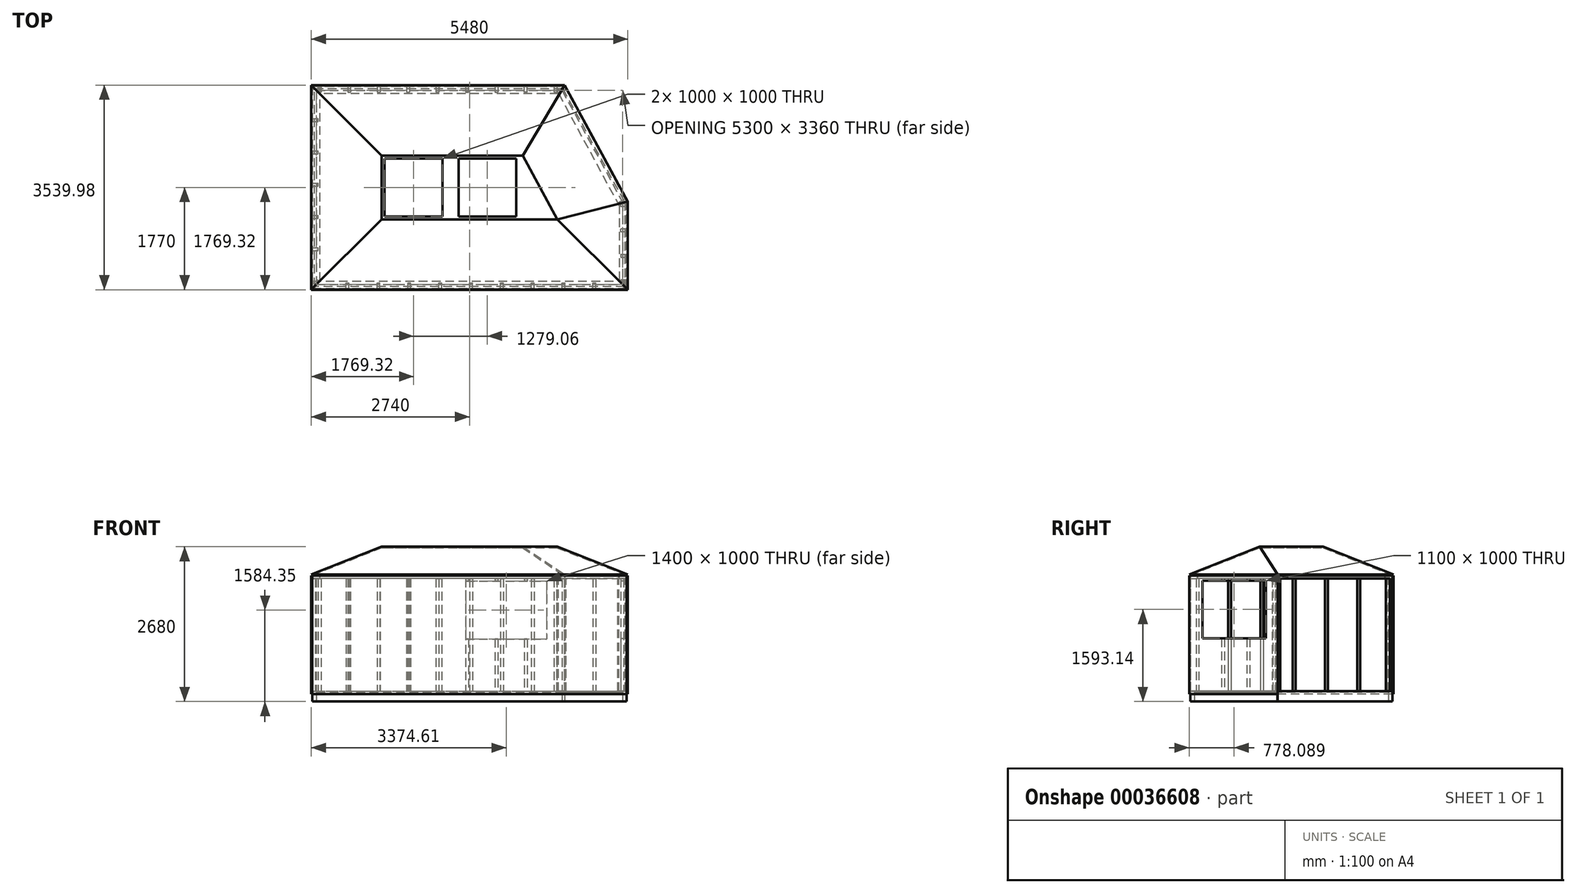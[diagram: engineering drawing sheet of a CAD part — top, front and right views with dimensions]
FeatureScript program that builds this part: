
annotation { "Feature Type Name" : "Feature", "Feature Type Description" : "" }
export const myFeature = defineFeature(function(context is Context, id is Id, definition is map)
    precondition{}
    {
        {
            var Q0;
            Q0=qCreatedBy(makeId("Top.planeOp"),FACE);
            var sketch = newSketch(context, id + "F0", { "sketchPlane" : qUnion([Q0])});
            skLineSegment(sketch, "E0.bottom", {"start": v(0, 0) * mm, "end": v(4365, 0) * mm});
            skLineSegment(sketch, "E0.top", {"start": v(0, -3500) * mm, "end": v(5440, -3500) * mm});
            skLineSegment(sketch, "E0.left", {"start": v(0, 0) * mm, "end": v(0, -3500) * mm});
            skLineSegment(sketch, "E0.right", {"start": v(5440, -1990) * mm, "end": v(5440, -3500) * mm});
            skLineSegment(sketch, "E1", {"start": v(4365, 0) * mm, "end": v(5440, -1990) * mm});
            skLineSegment(sketch, "E2.0", {"start": v(70, -70) * mm, "end": v(70, -3430) * mm});
            skLineSegment(sketch, "E2.1", {"start": v(70, -70) * mm, "end": v(4323.25, -70) * mm});
            skLineSegment(sketch, "E2.2", {"start": v(4323.25, -70) * mm, "end": v(5370, -2007.7) * mm});
            skLineSegment(sketch, "E2.3", {"start": v(5370, -2007.7) * mm, "end": v(5370, -3430) * mm});
            skLineSegment(sketch, "E2.4", {"start": v(70, -3430) * mm, "end": v(5370, -3430) * mm});
            skSolve(sketch);
        }
        {
            var Q0;
            Q0=makeQuery(id+"F0.imprint","IMPRINT",FACE,{"disambiguationData":[TD([[makeQuery(id+"F0.imprint","IMPRINT",EDGE,{"derivedFrom":sQuery(id+"F0.wireOp",EDGE,"E0.bottom")}),-1.0]])]});
            extrude(context, id + "F1", {"entities" : qUnion([Q0]), "depth" : 180 * mm});
        }
        {
            var Q0;
            Q0=makeQuery(id+"F0.imprint","IMPRINT",FACE,{"disambiguationData":[TD([[makeQuery(id+"F0.imprint","IMPRINT",EDGE,{"derivedFrom":sQuery(id+"F0.wireOp",EDGE,"E2.0")}),1.0]])]});
            extrude(context, id + "F2", {"entities" : qUnion([Q0]), "depth" : 180 * mm, "hasSecondDirection" : true, "secondDirectionOppositeDirection" : false, "secondDirectionDepth" : 160 * mm});
        }
        {
            var Q0;
            Q0=makeQuery(id+"F1.opExtrude","CAP_FACE",FACE,{"disambiguationData":[OSD([sQuery(id+"F0.wireOp",EDGE,"E0.bottom"),sQuery(id+"F0.wireOp",EDGE,"E0.top"),sQuery(id+"F0.wireOp",EDGE,"E0.left"),sQuery(id+"F0.wireOp",EDGE,"E0.right"),sQuery(id+"F0.wireOp",EDGE,"E1"),sQuery(id+"F0.wireOp",EDGE,"E2.0"),sQuery(id+"F0.wireOp",EDGE,"E2.1"),sQuery(id+"F0.wireOp",EDGE,"E2.2"),sQuery(id+"F0.wireOp",EDGE,"E2.3"),sQuery(id+"F0.wireOp",EDGE,"E2.4")])],"isStart":false});
            var sketch = newSketch(context, id + "F3", { "sketchPlane" : qUnion([Q0])});
            skLineSegment(sketch, "E3.bottom", {"start": v(0, -3500) * mm, "end": v(50, -3500) * mm});
            skLineSegment(sketch, "E3.top", {"start": v(0, -3400) * mm, "end": v(50, -3400) * mm});
            skLineSegment(sketch, "E3.left", {"start": v(0, -3500) * mm, "end": v(0, -3400) * mm});
            skLineSegment(sketch, "E3.right", {"start": v(50, -3500) * mm, "end": v(50, -3400) * mm});
            skLineSegment(sketch, "E4.bottom", {"start": v(50, -3500) * mm, "end": v(100, -3500) * mm});
            skLineSegment(sketch, "E4.top", {"start": v(50, -3400) * mm, "end": v(100, -3400) * mm});
            skLineSegment(sketch, "E4.right", {"start": v(100, -3500) * mm, "end": v(100, -3400) * mm});
            skLineSegment(sketch, "E5.1.0.0", {"start": v(584, -3400) * mm, "end": v(634, -3400) * mm});
            skLineSegment(sketch, "E5.1.0.1", {"start": v(584, -3500) * mm, "end": v(584, -3400) * mm});
            skLineSegment(sketch, "E5.1.0.2", {"start": v(584, -3500) * mm, "end": v(634, -3500) * mm});
            skLineSegment(sketch, "E5.1.0.3", {"start": v(634, -3500) * mm, "end": v(634, -3400) * mm});
            skLineSegment(sketch, "E5.2.0.0", {"start": v(1118, -3400) * mm, "end": v(1168, -3400) * mm});
            skLineSegment(sketch, "E5.2.0.1", {"start": v(1118, -3500) * mm, "end": v(1118, -3400) * mm});
            skLineSegment(sketch, "E5.2.0.2", {"start": v(1118, -3500) * mm, "end": v(1168, -3500) * mm});
            skLineSegment(sketch, "E5.2.0.3", {"start": v(1168, -3500) * mm, "end": v(1168, -3400) * mm});
            skLineSegment(sketch, "E5.3.0.0", {"start": v(1652, -3400) * mm, "end": v(1702, -3400) * mm});
            skLineSegment(sketch, "E5.3.0.1", {"start": v(1652, -3500) * mm, "end": v(1652, -3400) * mm});
            skLineSegment(sketch, "E5.3.0.2", {"start": v(1652, -3500) * mm, "end": v(1702, -3500) * mm});
            skLineSegment(sketch, "E5.3.0.3", {"start": v(1702, -3500) * mm, "end": v(1702, -3400) * mm});
            skLineSegment(sketch, "E5.4.0.0", {"start": v(2186, -3400) * mm, "end": v(2236, -3400) * mm});
            skLineSegment(sketch, "E5.4.0.1", {"start": v(2186, -3500) * mm, "end": v(2186, -3400) * mm});
            skLineSegment(sketch, "E5.4.0.2", {"start": v(2186, -3500) * mm, "end": v(2236, -3500) * mm});
            skLineSegment(sketch, "E5.4.0.3", {"start": v(2236, -3500) * mm, "end": v(2236, -3400) * mm});
            skLineSegment(sketch, "E5.5.0.0", {"start": v(2720, -3400) * mm, "end": v(2770, -3400) * mm});
            skLineSegment(sketch, "E5.5.0.1", {"start": v(2720, -3500) * mm, "end": v(2720, -3400) * mm});
            skLineSegment(sketch, "E5.5.0.2", {"start": v(2720, -3500) * mm, "end": v(2770, -3500) * mm});
            skLineSegment(sketch, "E5.5.0.3", {"start": v(2770, -3500) * mm, "end": v(2770, -3400) * mm});
            skLineSegment(sketch, "E5.6.0.0", {"start": v(3254, -3400) * mm, "end": v(3304, -3400) * mm});
            skLineSegment(sketch, "E5.6.0.1", {"start": v(3254, -3500) * mm, "end": v(3254, -3400) * mm});
            skLineSegment(sketch, "E5.6.0.2", {"start": v(3254, -3500) * mm, "end": v(3304, -3500) * mm});
            skLineSegment(sketch, "E5.6.0.3", {"start": v(3304, -3500) * mm, "end": v(3304, -3400) * mm});
            skLineSegment(sketch, "E5.7.0.0", {"start": v(3788, -3400) * mm, "end": v(3838, -3400) * mm});
            skLineSegment(sketch, "E5.7.0.1", {"start": v(3788, -3500) * mm, "end": v(3788, -3400) * mm});
            skLineSegment(sketch, "E5.7.0.2", {"start": v(3788, -3500) * mm, "end": v(3838, -3500) * mm});
            skLineSegment(sketch, "E5.7.0.3", {"start": v(3838, -3500) * mm, "end": v(3838, -3400) * mm});
            skLineSegment(sketch, "E5.8.0.0", {"start": v(4322, -3400) * mm, "end": v(4372, -3400) * mm});
            skLineSegment(sketch, "E5.8.0.1", {"start": v(4322, -3500) * mm, "end": v(4322, -3400) * mm});
            skLineSegment(sketch, "E5.8.0.2", {"start": v(4322, -3500) * mm, "end": v(4372, -3500) * mm});
            skLineSegment(sketch, "E5.8.0.3", {"start": v(4372, -3500) * mm, "end": v(4372, -3400) * mm});
            skLineSegment(sketch, "E5.9.0.0", {"start": v(4856, -3400) * mm, "end": v(4906, -3400) * mm});
            skLineSegment(sketch, "E5.9.0.1", {"start": v(4856, -3500) * mm, "end": v(4856, -3400) * mm});
            skLineSegment(sketch, "E5.9.0.2", {"start": v(4856, -3500) * mm, "end": v(4906, -3500) * mm});
            skLineSegment(sketch, "E5.9.0.3", {"start": v(4906, -3500) * mm, "end": v(4906, -3400) * mm});
            skLineSegment(sketch, "E5.10.0.0", {"start": v(5390, -3400) * mm, "end": v(5440, -3400) * mm});
            skLineSegment(sketch, "E5.10.0.1", {"start": v(5390, -3500) * mm, "end": v(5390, -3400) * mm});
            skLineSegment(sketch, "E5.10.0.2", {"start": v(5390, -3500) * mm, "end": v(5440, -3500) * mm});
            skLineSegment(sketch, "E5.10.0.3", {"start": v(5440, -3500) * mm, "end": v(5440, -3400) * mm});
            skLineSegment(sketch, "E5.direction1", {"start": v(50, -3500) * mm, "end": v(584, -3500) * mm, "construction": true});
            skLineSegment(sketch, "E6.bottom", {"start": v(5440, -3500) * mm, "end": v(0, -3500) * mm});
            skLineSegment(sketch, "E6.top", {"start": v(5440, -3520) * mm, "end": v(0, -3520) * mm});
            skLineSegment(sketch, "E6.left", {"start": v(5440, -3500) * mm, "end": v(5440, -3520) * mm});
            skLineSegment(sketch, "E6.right", {"start": v(0, -3500) * mm, "end": v(0, -3520) * mm});
            skLineSegment(sketch, "E7.bottom", {"start": v(0, -3400) * mm, "end": v(100, -3400) * mm});
            skLineSegment(sketch, "E7.top", {"start": v(0, -3350) * mm, "end": v(100, -3350) * mm});
            skLineSegment(sketch, "E7.left", {"start": v(0, -3400) * mm, "end": v(0, -3350) * mm});
            skLineSegment(sketch, "E7.right", {"start": v(100, -3400) * mm, "end": v(100, -3350) * mm});
            skLineSegment(sketch, "E8.0.1.0", {"start": v(0, -2841.67) * mm, "end": v(0, -2791.67) * mm});
            skLineSegment(sketch, "E8.0.1.1", {"start": v(100, -2841.67) * mm, "end": v(100, -2791.67) * mm});
            skLineSegment(sketch, "E8.0.1.2", {"start": v(0, -2841.67) * mm, "end": v(100, -2841.67) * mm});
            skLineSegment(sketch, "E8.0.1.3", {"start": v(0, -2791.67) * mm, "end": v(100, -2791.67) * mm});
            skLineSegment(sketch, "E8.0.2.0", {"start": v(0, -2283.34) * mm, "end": v(0, -2233.34) * mm});
            skLineSegment(sketch, "E8.0.2.1", {"start": v(100, -2283.34) * mm, "end": v(100, -2233.34) * mm});
            skLineSegment(sketch, "E8.0.2.2", {"start": v(0, -2283.34) * mm, "end": v(100, -2283.34) * mm});
            skLineSegment(sketch, "E8.0.2.3", {"start": v(0, -2233.34) * mm, "end": v(100, -2233.34) * mm});
            skLineSegment(sketch, "E8.0.3.0", {"start": v(0, -1725) * mm, "end": v(0, -1675) * mm});
            skLineSegment(sketch, "E8.0.3.1", {"start": v(100, -1725) * mm, "end": v(100, -1675) * mm});
            skLineSegment(sketch, "E8.0.3.2", {"start": v(0, -1725) * mm, "end": v(100, -1725) * mm});
            skLineSegment(sketch, "E8.0.3.3", {"start": v(0, -1675) * mm, "end": v(100, -1675) * mm});
            skLineSegment(sketch, "E8.0.4.0", {"start": v(0, -1166.68) * mm, "end": v(0, -1116.68) * mm});
            skLineSegment(sketch, "E8.0.4.1", {"start": v(100, -1166.68) * mm, "end": v(100, -1116.68) * mm});
            skLineSegment(sketch, "E8.0.4.2", {"start": v(0, -1166.68) * mm, "end": v(100, -1166.68) * mm});
            skLineSegment(sketch, "E8.0.4.3", {"start": v(0, -1116.68) * mm, "end": v(100, -1116.68) * mm});
            skLineSegment(sketch, "E8.0.5.0", {"start": v(0, -608.35) * mm, "end": v(0, -558.35) * mm});
            skLineSegment(sketch, "E8.0.5.1", {"start": v(100, -608.35) * mm, "end": v(100, -558.35) * mm});
            skLineSegment(sketch, "E8.0.5.2", {"start": v(0, -608.35) * mm, "end": v(100, -608.35) * mm});
            skLineSegment(sketch, "E8.0.5.3", {"start": v(0, -558.35) * mm, "end": v(100, -558.35) * mm});
            skLineSegment(sketch, "E8.0.6.0", {"start": v(0, -50.02) * mm, "end": v(0, -0.02) * mm});
            skLineSegment(sketch, "E8.0.6.1", {"start": v(100, -50.02) * mm, "end": v(100, -0.02) * mm});
            skLineSegment(sketch, "E8.0.6.2", {"start": v(0, -50.02) * mm, "end": v(100, -50.02) * mm});
            skLineSegment(sketch, "E8.0.6.3", {"start": v(0, -0.02) * mm, "end": v(100, -0.02) * mm});
            skLineSegment(sketch, "E8.direction1", {"start": v(0, -3400) * mm, "end": v(133.01, -3400) * mm, "construction": true});
            skLineSegment(sketch, "E8.direction2", {"start": v(0, -3400) * mm, "end": v(0, -2841.67) * mm, "construction": true});
            skLineSegment(sketch, "E9.bottom", {"start": v(-20, -0.02) * mm, "end": v(0, -0.02) * mm});
            skLineSegment(sketch, "E9.top", {"start": v(-20, -3520) * mm, "end": v(0, -3520) * mm});
            skLineSegment(sketch, "E9.left", {"start": v(-20, -0.02) * mm, "end": v(-20, -3520) * mm});
            skLineSegment(sketch, "E9.right", {"start": v(0, -0.02) * mm, "end": v(0, -3520) * mm});
            skSolve(sketch);
        }
        {
            var Q0;
            Q0=makeQuery(id+"F3.imprint","IMPRINT",FACE,{"disambiguationData":[TD([[makeQuery(id+"F3.imprint","IMPRINT",EDGE,{"derivedFrom":sQuery(id+"F3.wireOp",EDGE,"E5.10.0.0")}),-1.0]])]});
            var Q1;
            {var subQ3=sQuery(id+"F3.wireOp",EDGE,"E5.9.0.1");var subQ5=sQuery(id+"F3.wireOp",EDGE,"E6.bottom");var subQ7=makeQuery(id+"F3.imprint","INTERSECT",VERTEX,{"derivedFrom":[subQ3,subQ5]});Q1=makeQuery(id+"F3.imprint","IMPRINT",FACE,{"disambiguationData":[TD([[makeQuery(id+"F3.imprint","IMPRINT",EDGE,{"disambiguationData":[TD([[subQ7,-1.0]])],"derivedFrom":subQ3}),-1.0]])]});}
            var Q2;
            {var subQ3=sQuery(id+"F3.wireOp",EDGE,"E5.9.0.0");Q2=makeQuery(id+"F3.imprint","IMPRINT",FACE,{"disambiguationData":[TD([[makeQuery(id+"F3.imprint","IMPRINT",EDGE,{"derivedFrom":subQ3}),-1.0]])]});}
            var Q3;
            {var subQ3=sQuery(id+"F3.wireOp",EDGE,"E5.8.0.1");var subQ5=sQuery(id+"F3.wireOp",EDGE,"E6.bottom");var subQ7=makeQuery(id+"F3.imprint","INTERSECT",VERTEX,{"derivedFrom":[subQ3,subQ5]});Q3=makeQuery(id+"F3.imprint","IMPRINT",FACE,{"disambiguationData":[TD([[makeQuery(id+"F3.imprint","IMPRINT",EDGE,{"disambiguationData":[TD([[subQ7,-1.0]])],"derivedFrom":subQ3}),-1.0]])]});}
            var Q4;
            {var subQ5=sQuery(id+"F3.wireOp",EDGE,"E5.8.0.0");Q4=makeQuery(id+"F3.imprint","IMPRINT",FACE,{"disambiguationData":[TD([[makeQuery(id+"F3.imprint","IMPRINT",EDGE,{"derivedFrom":subQ5}),-1.0]])]});}
            var Q5;
            {var subQ0=sQuery(id+"F3.wireOp",EDGE,"E6.bottom");var subQ3=sQuery(id+"F3.wireOp",EDGE,"E5.7.0.1");var subQ4=makeQuery(id+"F3.imprint","INTERSECT",VERTEX,{"derivedFrom":[subQ3,subQ0]});Q5=makeQuery(id+"F3.imprint","IMPRINT",FACE,{"disambiguationData":[TD([[makeQuery(id+"F3.imprint","IMPRINT",EDGE,{"disambiguationData":[TD([[subQ4,-1.0]])],"derivedFrom":subQ3}),-1.0]])]});}
            var Q6;
            {var subQ3=sQuery(id+"F3.wireOp",EDGE,"E5.7.0.0");Q6=makeQuery(id+"F3.imprint","IMPRINT",FACE,{"disambiguationData":[TD([[makeQuery(id+"F3.imprint","IMPRINT",EDGE,{"derivedFrom":subQ3}),-1.0]])]});}
            var Q7;
            {var subQ3=sQuery(id+"F3.wireOp",EDGE,"E5.6.0.1");var subQ5=sQuery(id+"F3.wireOp",EDGE,"E6.bottom");var subQ7=makeQuery(id+"F3.imprint","INTERSECT",VERTEX,{"derivedFrom":[subQ3,subQ5]});Q7=makeQuery(id+"F3.imprint","IMPRINT",FACE,{"disambiguationData":[TD([[makeQuery(id+"F3.imprint","IMPRINT",EDGE,{"disambiguationData":[TD([[subQ7,-1.0]])],"derivedFrom":subQ3}),-1.0]])]});}
            var Q8;
            {var subQ5=sQuery(id+"F3.wireOp",EDGE,"E5.6.0.0");Q8=makeQuery(id+"F3.imprint","IMPRINT",FACE,{"disambiguationData":[TD([[makeQuery(id+"F3.imprint","IMPRINT",EDGE,{"derivedFrom":subQ5}),-1.0]])]});}
            var Q9;
            {var subQ3=sQuery(id+"F3.wireOp",EDGE,"E5.5.0.1");var subQ5=sQuery(id+"F3.wireOp",EDGE,"E6.bottom");var subQ7=makeQuery(id+"F3.imprint","INTERSECT",VERTEX,{"derivedFrom":[subQ3,subQ5]});Q9=makeQuery(id+"F3.imprint","IMPRINT",FACE,{"disambiguationData":[TD([[makeQuery(id+"F3.imprint","IMPRINT",EDGE,{"disambiguationData":[TD([[subQ7,-1.0]])],"derivedFrom":subQ3}),-1.0]])]});}
            var Q10;
            {var subQ5=sQuery(id+"F3.wireOp",EDGE,"E5.5.0.0");Q10=makeQuery(id+"F3.imprint","IMPRINT",FACE,{"disambiguationData":[TD([[makeQuery(id+"F3.imprint","IMPRINT",EDGE,{"derivedFrom":subQ5}),-1.0]])]});}
            var Q11;
            {var subQ3=sQuery(id+"F3.wireOp",EDGE,"E5.4.0.1");var subQ5=sQuery(id+"F3.wireOp",EDGE,"E6.bottom");var subQ7=makeQuery(id+"F3.imprint","INTERSECT",VERTEX,{"derivedFrom":[subQ3,subQ5]});Q11=makeQuery(id+"F3.imprint","IMPRINT",FACE,{"disambiguationData":[TD([[makeQuery(id+"F3.imprint","IMPRINT",EDGE,{"disambiguationData":[TD([[subQ7,-1.0]])],"derivedFrom":subQ3}),-1.0]])]});}
            var Q12;
            {var subQ5=sQuery(id+"F3.wireOp",EDGE,"E5.4.0.0");Q12=makeQuery(id+"F3.imprint","IMPRINT",FACE,{"disambiguationData":[TD([[makeQuery(id+"F3.imprint","IMPRINT",EDGE,{"derivedFrom":subQ5}),-1.0]])]});}
            var Q13;
            {var subQ3=sQuery(id+"F3.wireOp",EDGE,"E5.3.0.1");var subQ5=sQuery(id+"F3.wireOp",EDGE,"E6.bottom");var subQ7=makeQuery(id+"F3.imprint","INTERSECT",VERTEX,{"derivedFrom":[subQ3,subQ5]});Q13=makeQuery(id+"F3.imprint","IMPRINT",FACE,{"disambiguationData":[TD([[makeQuery(id+"F3.imprint","IMPRINT",EDGE,{"disambiguationData":[TD([[subQ7,-1.0]])],"derivedFrom":subQ3}),-1.0]])]});}
            var Q14;
            {var subQ5=sQuery(id+"F3.wireOp",EDGE,"E5.3.0.0");Q14=makeQuery(id+"F3.imprint","IMPRINT",FACE,{"disambiguationData":[TD([[makeQuery(id+"F3.imprint","IMPRINT",EDGE,{"derivedFrom":subQ5}),-1.0]])]});}
            var Q15;
            {var subQ3=sQuery(id+"F3.wireOp",EDGE,"E5.2.0.1");var subQ5=sQuery(id+"F3.wireOp",EDGE,"E6.bottom");var subQ7=makeQuery(id+"F3.imprint","INTERSECT",VERTEX,{"derivedFrom":[subQ3,subQ5]});Q15=makeQuery(id+"F3.imprint","IMPRINT",FACE,{"disambiguationData":[TD([[makeQuery(id+"F3.imprint","IMPRINT",EDGE,{"disambiguationData":[TD([[subQ7,-1.0]])],"derivedFrom":subQ3}),-1.0]])]});}
            var Q16;
            {var subQ5=sQuery(id+"F3.wireOp",EDGE,"E5.2.0.0");Q16=makeQuery(id+"F3.imprint","IMPRINT",FACE,{"disambiguationData":[TD([[makeQuery(id+"F3.imprint","IMPRINT",EDGE,{"derivedFrom":subQ5}),-1.0]])]});}
            var Q17;
            {var subQ0=sQuery(id+"F3.wireOp",EDGE,"E6.bottom");var subQ3=sQuery(id+"F3.wireOp",EDGE,"E5.1.0.1");var subQ4=makeQuery(id+"F3.imprint","INTERSECT",VERTEX,{"derivedFrom":[subQ3,subQ0]});Q17=makeQuery(id+"F3.imprint","IMPRINT",FACE,{"disambiguationData":[TD([[makeQuery(id+"F3.imprint","IMPRINT",EDGE,{"disambiguationData":[TD([[subQ4,-1.0]])],"derivedFrom":subQ3}),-1.0]])]});}
            var Q18;
            {var subQ5=sQuery(id+"F3.wireOp",EDGE,"E5.1.0.0");Q18=makeQuery(id+"F3.imprint","IMPRINT",FACE,{"disambiguationData":[TD([[makeQuery(id+"F3.imprint","IMPRINT",EDGE,{"derivedFrom":subQ5}),-1.0]])]});}
            extrude(context, id + "F4", {"entities" : qUnion([Q0, Q1, Q2, Q3, Q4, Q5, Q6, Q7, Q8, Q9, Q10, Q11, Q12, Q13, Q14, Q15, Q16, Q17, Q18]), "depth" : 1950 * mm});
        }
        {
            var Q0;
            {var subQ5=sQuery(id+"F3.wireOp",EDGE,"E3.right");Q0=makeQuery(id+"F3.imprint","IMPRINT",FACE,{"disambiguationData":[TD([[makeQuery(id+"F3.imprint","IMPRINT",EDGE,{"derivedFrom":subQ5}),1.0]])]});}
            extrude(context, id + "F5", {"entities" : qUnion([Q0]), "depth" : 1950 * mm});
        }
        {
            var Q0;
            {var subQ0=sQuery(id+"F3.wireOp",EDGE,"E7.right");Q0=makeQuery(id+"F3.imprint","IMPRINT",FACE,{"disambiguationData":[TD([[makeQuery(id+"F3.imprint","IMPRINT",EDGE,{"derivedFrom":subQ0}),1.0]])]});}
            var Q1;
            {var subQ3=sQuery(id+"F3.wireOp",EDGE,"E7.bottom");var subQ5=makeQuery(id+"F3.imprint","INTERSECT",VERTEX,{"derivedFrom":[sQuery(id+"F3.wireOp",EDGE,"E3.right"),subQ3]});Q1=makeQuery(id+"F3.imprint","IMPRINT",FACE,{"disambiguationData":[TD([[makeQuery(id+"F3.imprint","IMPRINT",EDGE,{"disambiguationData":[TD([[subQ5,1.0]])],"derivedFrom":subQ3}),1.0]])]});}
            var Q2;
            {var subQ3=sQuery(id+"F3.wireOp",EDGE,"E8.0.1.2");var subQ5=sQuery(id+"F3.wireOp",EDGE,"E9.right");var subQ7=makeQuery(id+"F3.imprint","INTERSECT",VERTEX,{"derivedFrom":[subQ3,subQ5]});Q2=makeQuery(id+"F3.imprint","IMPRINT",FACE,{"disambiguationData":[TD([[makeQuery(id+"F3.imprint","IMPRINT",EDGE,{"disambiguationData":[TD([[subQ7,-1.0]])],"derivedFrom":subQ3}),1.0]])]});}
            var Q3;
            {var subQ5=sQuery(id+"F3.wireOp",EDGE,"E8.0.1.1");Q3=makeQuery(id+"F3.imprint","IMPRINT",FACE,{"disambiguationData":[TD([[makeQuery(id+"F3.imprint","IMPRINT",EDGE,{"derivedFrom":subQ5}),1.0]])]});}
            var Q4;
            {var subQ3=sQuery(id+"F3.wireOp",EDGE,"E8.0.2.2");var subQ5=sQuery(id+"F3.wireOp",EDGE,"E9.right");var subQ7=makeQuery(id+"F3.imprint","INTERSECT",VERTEX,{"derivedFrom":[subQ3,subQ5]});Q4=makeQuery(id+"F3.imprint","IMPRINT",FACE,{"disambiguationData":[TD([[makeQuery(id+"F3.imprint","IMPRINT",EDGE,{"disambiguationData":[TD([[subQ7,-1.0]])],"derivedFrom":subQ3}),1.0]])]});}
            var Q5;
            {var subQ3=sQuery(id+"F3.wireOp",EDGE,"E8.0.2.1");Q5=makeQuery(id+"F3.imprint","IMPRINT",FACE,{"disambiguationData":[TD([[makeQuery(id+"F3.imprint","IMPRINT",EDGE,{"derivedFrom":subQ3}),1.0]])]});}
            var Q6;
            {var subQ3=sQuery(id+"F3.wireOp",EDGE,"E8.0.3.2");var subQ5=sQuery(id+"F3.wireOp",EDGE,"E9.right");var subQ7=makeQuery(id+"F3.imprint","INTERSECT",VERTEX,{"derivedFrom":[subQ3,subQ5]});Q6=makeQuery(id+"F3.imprint","IMPRINT",FACE,{"disambiguationData":[TD([[makeQuery(id+"F3.imprint","IMPRINT",EDGE,{"disambiguationData":[TD([[subQ7,-1.0]])],"derivedFrom":subQ3}),1.0]])]});}
            var Q7;
            {var subQ3=sQuery(id+"F3.wireOp",EDGE,"E8.0.3.1");Q7=makeQuery(id+"F3.imprint","IMPRINT",FACE,{"disambiguationData":[TD([[makeQuery(id+"F3.imprint","IMPRINT",EDGE,{"derivedFrom":subQ3}),1.0]])]});}
            var Q8;
            {var subQ3=sQuery(id+"F3.wireOp",EDGE,"E8.0.4.2");var subQ5=sQuery(id+"F3.wireOp",EDGE,"E9.right");var subQ7=makeQuery(id+"F3.imprint","INTERSECT",VERTEX,{"derivedFrom":[subQ3,subQ5]});Q8=makeQuery(id+"F3.imprint","IMPRINT",FACE,{"disambiguationData":[TD([[makeQuery(id+"F3.imprint","IMPRINT",EDGE,{"disambiguationData":[TD([[subQ7,-1.0]])],"derivedFrom":subQ3}),1.0]])]});}
            var Q9;
            {var subQ5=sQuery(id+"F3.wireOp",EDGE,"E8.0.4.1");Q9=makeQuery(id+"F3.imprint","IMPRINT",FACE,{"disambiguationData":[TD([[makeQuery(id+"F3.imprint","IMPRINT",EDGE,{"derivedFrom":subQ5}),1.0]])]});}
            var Q10;
            {var subQ0=sQuery(id+"F3.wireOp",EDGE,"E9.right");var subQ3=sQuery(id+"F3.wireOp",EDGE,"E8.0.5.2");var subQ4=makeQuery(id+"F3.imprint","INTERSECT",VERTEX,{"derivedFrom":[subQ3,subQ0]});Q10=makeQuery(id+"F3.imprint","IMPRINT",FACE,{"disambiguationData":[TD([[makeQuery(id+"F3.imprint","IMPRINT",EDGE,{"disambiguationData":[TD([[subQ4,-1.0]])],"derivedFrom":subQ3}),1.0]])]});}
            var Q11;
            {var subQ5=sQuery(id+"F3.wireOp",EDGE,"E8.0.5.1");Q11=makeQuery(id+"F3.imprint","IMPRINT",FACE,{"disambiguationData":[TD([[makeQuery(id+"F3.imprint","IMPRINT",EDGE,{"derivedFrom":subQ5}),1.0]])]});}
            var Q12;
            Q12=makeQuery(id+"F3.imprint","IMPRINT",FACE,{"disambiguationData":[TD([[makeQuery(id+"F3.imprint","IMPRINT",EDGE,{"derivedFrom":sQuery(id+"F3.wireOp",EDGE,"E8.0.6.1")}),1.0]])]});
            extrude(context, id + "F6", {"entities" : qUnion([Q0, Q1, Q2, Q3, Q4, Q5, Q6, Q7, Q8, Q9, Q10, Q11, Q12]), "depth" : 1950 * mm});
        }
        {
            var Q0;
            {var subQ2=sQuery(id+"F3.wireOp",EDGE,"E6.top");Q0=makeQuery(id+"F3.imprint","IMPRINT",FACE,{"disambiguationData":[TD([[makeQuery(id+"F3.imprint","IMPRINT",EDGE,{"derivedFrom":subQ2}),-1.0]])]});}
            extrude(context, id + "F7", {"entities" : qUnion([Q0]), "depth" : 2000 * mm, "hasSecondDirection" : true, "secondDirectionOppositeDirection" : true, "secondDirectionDepth" : 50 * mm});
        }
        {
            var Q0;
            {var subQ9=sQuery(id+"F3.wireOp",EDGE,"E9.bottom");Q0=makeQuery(id+"F3.imprint","IMPRINT",FACE,{"disambiguationData":[TD([[makeQuery(id+"F3.imprint","IMPRINT",EDGE,{"derivedFrom":subQ9}),-1.0]])]});}
            extrude(context, id + "F8", {"entities" : qUnion([Q0]), "depth" : 2000 * mm, "hasSecondDirection" : true, "secondDirectionOppositeDirection" : true, "secondDirectionDepth" : 50 * mm});
        }
        {
            var Q0;
            Q0=makeQuery(id+"F8.opExtrude","SWEPT_FACE",FACE,{"disambiguationData":[OSD([sQuery(id+"F3.wireOp",EDGE,"E9.right")])]});
            var sketch = newSketch(context, id + "F9", { "sketchPlane" : qUnion([Q0])});
            skLineSegment(sketch, "E10.bottom", {"start": v(-3500, 2180) * mm, "end": v(-3375, 2180) * mm});
            skLineSegment(sketch, "E10.top", {"start": v(-3500, 2130) * mm, "end": v(-3375, 2130) * mm});
            skLineSegment(sketch, "E10.left", {"start": v(-3500, 2180) * mm, "end": v(-3500, 2130) * mm});
            skLineSegment(sketch, "E10.right", {"start": v(-3375, 2180) * mm, "end": v(-3375, 2130) * mm});
            skSolve(sketch);
        }
        {
            var Q0;
            Q0=makeQuery(id+"F9.imprint","IMPRINT",FACE,{"disambiguationData":[TD([[makeQuery(id+"F9.imprint","IMPRINT",EDGE,{"derivedFrom":sQuery(id+"F9.wireOp",EDGE,"E10.bottom")}),1.0]])]});
            extrude(context, id + "F10", {"entities" : qUnion([Q0]), "depth" : 5440 * mm});
        }
        {
            var Q0;
            Q0=makeQuery(id+"F10.opExtrude","SWEPT_FACE",FACE,{"disambiguationData":[OSD([sQuery(id+"F9.wireOp",EDGE,"E10.right")])]});
            var sketch = newSketch(context, id + "F11", { "sketchPlane" : qUnion([Q0])});
            skLineSegment(sketch, "E11.bottom", {"start": v(0, 2180) * mm, "end": v(-125, 2180) * mm});
            skLineSegment(sketch, "E11.top", {"start": v(0, 2130) * mm, "end": v(-125, 2130) * mm});
            skLineSegment(sketch, "E11.left", {"start": v(0, 2180) * mm, "end": v(0, 2130) * mm});
            skLineSegment(sketch, "E11.right", {"start": v(-125, 2180) * mm, "end": v(-125, 2130) * mm});
            skSolve(sketch);
        }
        {
            var Q0;
            Q0=makeQuery(id+"F11.imprint","IMPRINT",FACE,{"disambiguationData":[TD([[makeQuery(id+"F11.imprint","IMPRINT",EDGE,{"derivedFrom":sQuery(id+"F11.wireOp",EDGE,"E11.bottom")}),-1.0]])]});
            extrude(context, id + "F12", {"entities" : qUnion([Q0]), "depth" : 3375 * mm});
        }
        {
            var Q0;
            Q0=makeQuery(id+"F1.opExtrude","CAP_FACE",FACE,{"disambiguationData":[OSD([sQuery(id+"F0.wireOp",EDGE,"E0.bottom"),sQuery(id+"F0.wireOp",EDGE,"E0.top"),sQuery(id+"F0.wireOp",EDGE,"E0.left"),sQuery(id+"F0.wireOp",EDGE,"E0.right"),sQuery(id+"F0.wireOp",EDGE,"E1"),sQuery(id+"F0.wireOp",EDGE,"E2.0"),sQuery(id+"F0.wireOp",EDGE,"E2.1"),sQuery(id+"F0.wireOp",EDGE,"E2.2"),sQuery(id+"F0.wireOp",EDGE,"E2.3"),sQuery(id+"F0.wireOp",EDGE,"E2.4")])],"isStart":false});
            var sketch = newSketch(context, id + "F13", { "sketchPlane" : qUnion([Q0])});
            skLineSegment(sketch, "E12.bottom", {"start": v(100, -0.02) * mm, "end": v(150, -0.02) * mm});
            skLineSegment(sketch, "E12.top", {"start": v(100, -100.02) * mm, "end": v(150, -100.02) * mm});
            skLineSegment(sketch, "E12.left", {"start": v(100, -0.02) * mm, "end": v(100, -100.02) * mm});
            skLineSegment(sketch, "E12.right", {"start": v(150, -0.02) * mm, "end": v(150, -100.02) * mm});
            skLineSegment(sketch, "E13.1.0.0", {"start": v(610, -0.02) * mm, "end": v(660, -0.02) * mm});
            skLineSegment(sketch, "E13.1.0.1", {"start": v(610, -100.02) * mm, "end": v(660, -100.02) * mm});
            skLineSegment(sketch, "E13.1.0.2", {"start": v(610, -0.02) * mm, "end": v(610, -100.02) * mm});
            skLineSegment(sketch, "E13.1.0.3", {"start": v(660, -0.02) * mm, "end": v(660, -100.02) * mm});
            skLineSegment(sketch, "E13.2.0.0", {"start": v(1120, -0.01) * mm, "end": v(1170, -0.01) * mm});
            skLineSegment(sketch, "E13.2.0.1", {"start": v(1120, -100.01) * mm, "end": v(1170, -100.01) * mm});
            skLineSegment(sketch, "E13.2.0.2", {"start": v(1120, -0.01) * mm, "end": v(1120, -100.01) * mm});
            skLineSegment(sketch, "E13.2.0.3", {"start": v(1170, -0.01) * mm, "end": v(1170, -100.01) * mm});
            skLineSegment(sketch, "E13.3.0.0", {"start": v(1630, -0.01) * mm, "end": v(1680, -0.01) * mm});
            skLineSegment(sketch, "E13.3.0.1", {"start": v(1630, -100.01) * mm, "end": v(1680, -100.01) * mm});
            skLineSegment(sketch, "E13.3.0.2", {"start": v(1630, -0.01) * mm, "end": v(1630, -100.01) * mm});
            skLineSegment(sketch, "E13.3.0.3", {"start": v(1680, -0.01) * mm, "end": v(1680, -100.01) * mm});
            skLineSegment(sketch, "E13.4.0.0", {"start": v(2140, 0) * mm, "end": v(2190, 0) * mm});
            skLineSegment(sketch, "E13.4.0.1", {"start": v(2140, -100) * mm, "end": v(2190, -100) * mm});
            skLineSegment(sketch, "E13.4.0.2", {"start": v(2140, 0) * mm, "end": v(2140, -100) * mm});
            skLineSegment(sketch, "E13.4.0.3", {"start": v(2190, 0) * mm, "end": v(2190, -100) * mm});
            skLineSegment(sketch, "E13.5.0.0", {"start": v(2650, 0) * mm, "end": v(2700, 0) * mm});
            skLineSegment(sketch, "E13.5.0.1", {"start": v(2650, -100) * mm, "end": v(2700, -100) * mm});
            skLineSegment(sketch, "E13.5.0.2", {"start": v(2650, 0) * mm, "end": v(2650, -100) * mm});
            skLineSegment(sketch, "E13.5.0.3", {"start": v(2700, 0) * mm, "end": v(2700, -100) * mm});
            skLineSegment(sketch, "E13.6.0.0", {"start": v(3160, 0) * mm, "end": v(3210, 0) * mm});
            skLineSegment(sketch, "E13.6.0.1", {"start": v(3160, -100) * mm, "end": v(3210, -100) * mm});
            skLineSegment(sketch, "E13.6.0.2", {"start": v(3160, 0) * mm, "end": v(3160, -100) * mm});
            skLineSegment(sketch, "E13.6.0.3", {"start": v(3210, 0) * mm, "end": v(3210, -100) * mm});
            skLineSegment(sketch, "E13.7.0.0", {"start": v(3670, 0) * mm, "end": v(3720, 0) * mm});
            skLineSegment(sketch, "E13.7.0.1", {"start": v(3670, -100) * mm, "end": v(3720, -100) * mm});
            skLineSegment(sketch, "E13.7.0.2", {"start": v(3670, 0) * mm, "end": v(3670, -100) * mm});
            skLineSegment(sketch, "E13.7.0.3", {"start": v(3720, 0) * mm, "end": v(3720, -100) * mm});
            skLineSegment(sketch, "E13.8.0.0", {"start": v(4180, 0) * mm, "end": v(4230, 0) * mm});
            skLineSegment(sketch, "E13.8.0.1", {"start": v(4180, -100) * mm, "end": v(4230, -100) * mm});
            skLineSegment(sketch, "E13.8.0.2", {"start": v(4180, 0) * mm, "end": v(4180, -100) * mm});
            skLineSegment(sketch, "E13.8.0.3", {"start": v(4230, 0) * mm, "end": v(4230, -100) * mm});
            skLineSegment(sketch, "E13.direction1", {"start": v(100, -100.02) * mm, "end": v(610, -100.02) * mm, "construction": true});
            skSolve(sketch);
        }
        {
            var Q0;
            {var subQ5=sQuery(id+"F13.wireOp",EDGE,"E12.bottom");Q0=makeQuery(id+"F13.imprint","IMPRINT",FACE,{"disambiguationData":[TD([[makeQuery(id+"F13.imprint","IMPRINT",EDGE,{"derivedFrom":subQ5}),-1.0]])]});}
            var Q1;
            {var subQ5=sQuery(id+"F13.wireOp",EDGE,"E12.top");Q1=makeQuery(id+"F13.imprint","IMPRINT",FACE,{"disambiguationData":[TD([[makeQuery(id+"F13.imprint","IMPRINT",EDGE,{"derivedFrom":subQ5}),1.0]])]});}
            var Q2;
            {var subQ5=sQuery(id+"F13.wireOp",EDGE,"E13.1.0.0");Q2=makeQuery(id+"F13.imprint","IMPRINT",FACE,{"disambiguationData":[TD([[makeQuery(id+"F13.imprint","IMPRINT",EDGE,{"derivedFrom":subQ5}),-1.0]])]});}
            var Q3;
            {var subQ5=sQuery(id+"F13.wireOp",EDGE,"E13.1.0.1");Q3=makeQuery(id+"F13.imprint","IMPRINT",FACE,{"disambiguationData":[TD([[makeQuery(id+"F13.imprint","IMPRINT",EDGE,{"derivedFrom":subQ5}),1.0]])]});}
            var Q4;
            {var subQ5=sQuery(id+"F13.wireOp",EDGE,"E13.2.0.0");Q4=makeQuery(id+"F13.imprint","IMPRINT",FACE,{"disambiguationData":[TD([[makeQuery(id+"F13.imprint","IMPRINT",EDGE,{"derivedFrom":subQ5}),-1.0]])]});}
            var Q5;
            {var subQ5=sQuery(id+"F13.wireOp",EDGE,"E13.2.0.1");Q5=makeQuery(id+"F13.imprint","IMPRINT",FACE,{"disambiguationData":[TD([[makeQuery(id+"F13.imprint","IMPRINT",EDGE,{"derivedFrom":subQ5}),1.0]])]});}
            var Q6;
            {var subQ5=sQuery(id+"F13.wireOp",EDGE,"E13.3.0.0");Q6=makeQuery(id+"F13.imprint","IMPRINT",FACE,{"disambiguationData":[TD([[makeQuery(id+"F13.imprint","IMPRINT",EDGE,{"derivedFrom":subQ5}),-1.0]])]});}
            var Q7;
            {var subQ5=sQuery(id+"F13.wireOp",EDGE,"E13.3.0.1");Q7=makeQuery(id+"F13.imprint","IMPRINT",FACE,{"disambiguationData":[TD([[makeQuery(id+"F13.imprint","IMPRINT",EDGE,{"derivedFrom":subQ5}),1.0]])]});}
            var Q8;
            {var subQ5=sQuery(id+"F13.wireOp",EDGE,"E13.4.0.0");Q8=makeQuery(id+"F13.imprint","IMPRINT",FACE,{"disambiguationData":[TD([[makeQuery(id+"F13.imprint","IMPRINT",EDGE,{"derivedFrom":subQ5}),-1.0]])]});}
            var Q9;
            {var subQ5=sQuery(id+"F13.wireOp",EDGE,"E13.4.0.1");Q9=makeQuery(id+"F13.imprint","IMPRINT",FACE,{"disambiguationData":[TD([[makeQuery(id+"F13.imprint","IMPRINT",EDGE,{"derivedFrom":subQ5}),1.0]])]});}
            var Q10;
            {var subQ3=sQuery(id+"F13.wireOp",EDGE,"E13.5.0.0");Q10=makeQuery(id+"F13.imprint","IMPRINT",FACE,{"disambiguationData":[TD([[makeQuery(id+"F13.imprint","IMPRINT",EDGE,{"derivedFrom":subQ3}),-1.0]])]});}
            var Q11;
            {var subQ3=sQuery(id+"F13.wireOp",EDGE,"E13.5.0.1");Q11=makeQuery(id+"F13.imprint","IMPRINT",FACE,{"disambiguationData":[TD([[makeQuery(id+"F13.imprint","IMPRINT",EDGE,{"derivedFrom":subQ3}),1.0]])]});}
            var Q12;
            {var subQ5=sQuery(id+"F13.wireOp",EDGE,"E13.6.0.0");Q12=makeQuery(id+"F13.imprint","IMPRINT",FACE,{"disambiguationData":[TD([[makeQuery(id+"F13.imprint","IMPRINT",EDGE,{"derivedFrom":subQ5}),-1.0]])]});}
            var Q13;
            {var subQ5=sQuery(id+"F13.wireOp",EDGE,"E13.6.0.1");Q13=makeQuery(id+"F13.imprint","IMPRINT",FACE,{"disambiguationData":[TD([[makeQuery(id+"F13.imprint","IMPRINT",EDGE,{"derivedFrom":subQ5}),1.0]])]});}
            var Q14;
            {var subQ5=sQuery(id+"F13.wireOp",EDGE,"E13.7.0.0");Q14=makeQuery(id+"F13.imprint","IMPRINT",FACE,{"disambiguationData":[TD([[makeQuery(id+"F13.imprint","IMPRINT",EDGE,{"derivedFrom":subQ5}),-1.0]])]});}
            var Q15;
            {var subQ5=sQuery(id+"F13.wireOp",EDGE,"E13.7.0.1");Q15=makeQuery(id+"F13.imprint","IMPRINT",FACE,{"disambiguationData":[TD([[makeQuery(id+"F13.imprint","IMPRINT",EDGE,{"derivedFrom":subQ5}),1.0]])]});}
            var Q16;
            {var subQ6=sQuery(id+"F13.wireOp",EDGE,"E13.8.0.0");Q16=makeQuery(id+"F13.imprint","IMPRINT",FACE,{"disambiguationData":[TD([[makeQuery(id+"F13.imprint","IMPRINT",EDGE,{"derivedFrom":subQ6}),-1.0]])]});}
            var Q17;
            {var subQ5=sQuery(id+"F13.wireOp",EDGE,"E13.8.0.1");Q17=makeQuery(id+"F13.imprint","IMPRINT",FACE,{"disambiguationData":[TD([[makeQuery(id+"F13.imprint","IMPRINT",EDGE,{"derivedFrom":subQ5}),1.0]])]});}
            extrude(context, id + "F14", {"entities" : qUnion([Q0, Q1, Q2, Q3, Q4, Q5, Q6, Q7, Q8, Q9, Q10, Q11, Q12, Q13, Q14, Q15, Q16, Q17]), "depth" : 1950 * mm});
        }
        {
            var Q0;
            Q0=makeQuery(id+"F12.opExtrude","SWEPT_FACE",FACE,{"disambiguationData":[OSD([sQuery(id+"F11.wireOp",EDGE,"E11.right")])]});
            var sketch = newSketch(context, id + "F15", { "sketchPlane" : qUnion([Q0])});
            skLineSegment(sketch, "E14.bottom", {"start": v(0, 2180) * mm, "end": v(-125, 2180) * mm});
            skLineSegment(sketch, "E14.top", {"start": v(0, 2130) * mm, "end": v(-125, 2130) * mm});
            skLineSegment(sketch, "E14.left", {"start": v(0, 2180) * mm, "end": v(0, 2130) * mm});
            skLineSegment(sketch, "E14.right", {"start": v(-125, 2180) * mm, "end": v(-125, 2130) * mm});
            skSolve(sketch);
        }
        {
            var Q0;
            Q0=makeQuery(id+"F15.imprint","IMPRINT",FACE,{"disambiguationData":[TD([[makeQuery(id+"F15.imprint","IMPRINT",EDGE,{"derivedFrom":sQuery(id+"F15.wireOp",EDGE,"E14.bottom")}),1.0]])]});
            extrude(context, id + "F16", {"entities" : qUnion([Q0]), "depth" : 4240 * mm});
        }
        {
            var Q0;
            Q0=makeQuery(id+"F1.opExtrude","CAP_FACE",FACE,{"disambiguationData":[OSD([sQuery(id+"F0.wireOp",EDGE,"E0.bottom"),sQuery(id+"F0.wireOp",EDGE,"E0.top"),sQuery(id+"F0.wireOp",EDGE,"E0.left"),sQuery(id+"F0.wireOp",EDGE,"E0.right"),sQuery(id+"F0.wireOp",EDGE,"E1"),sQuery(id+"F0.wireOp",EDGE,"E2.0"),sQuery(id+"F0.wireOp",EDGE,"E2.1"),sQuery(id+"F0.wireOp",EDGE,"E2.2"),sQuery(id+"F0.wireOp",EDGE,"E2.3"),sQuery(id+"F0.wireOp",EDGE,"E2.4")])],"isStart":false});
            var sketch = newSketch(context, id + "F17", { "sketchPlane" : qUnion([Q0])});
            skLineSegment(sketch, "E15.bottom", {"start": v(5440, -3400) * mm, "end": v(5340, -3400) * mm});
            skLineSegment(sketch, "E15.top", {"start": v(5440, -3350) * mm, "end": v(5340, -3350) * mm});
            skLineSegment(sketch, "E15.left", {"start": v(5440, -3400) * mm, "end": v(5440, -3350) * mm});
            skLineSegment(sketch, "E15.right", {"start": v(5340, -3400) * mm, "end": v(5340, -3350) * mm});
            skLineSegment(sketch, "E16.0.1.0", {"start": v(5440, -2910) * mm, "end": v(5340, -2910) * mm});
            skLineSegment(sketch, "E16.0.1.1", {"start": v(5340, -2960) * mm, "end": v(5340, -2910) * mm});
            skLineSegment(sketch, "E16.0.1.2", {"start": v(5440, -2960) * mm, "end": v(5340, -2960) * mm});
            skLineSegment(sketch, "E16.0.1.3", {"start": v(5440, -2960) * mm, "end": v(5440, -2910) * mm});
            skLineSegment(sketch, "E16.0.2.0", {"start": v(5440, -2470) * mm, "end": v(5340, -2470) * mm});
            skLineSegment(sketch, "E16.0.2.1", {"start": v(5340, -2520) * mm, "end": v(5340, -2470) * mm});
            skLineSegment(sketch, "E16.0.2.2", {"start": v(5440, -2520) * mm, "end": v(5340, -2520) * mm});
            skLineSegment(sketch, "E16.0.2.3", {"start": v(5440, -2520) * mm, "end": v(5440, -2470) * mm});
            skLineSegment(sketch, "E16.0.3.0", {"start": v(5440, -2030) * mm, "end": v(5340, -2030) * mm});
            skLineSegment(sketch, "E16.0.3.1", {"start": v(5340, -2080) * mm, "end": v(5340, -2030) * mm});
            skLineSegment(sketch, "E16.0.3.2", {"start": v(5440, -2080) * mm, "end": v(5340, -2080) * mm});
            skLineSegment(sketch, "E16.0.3.3", {"start": v(5440, -2080) * mm, "end": v(5440, -2030) * mm});
            skLineSegment(sketch, "E16.direction1", {"start": v(5340, -3400) * mm, "end": v(5390, -3400) * mm, "construction": true});
            skLineSegment(sketch, "E16.direction2", {"start": v(5340, -3400) * mm, "end": v(5340, -2960) * mm, "construction": true});
            skSolve(sketch);
        }
        {
            var Q0;
            {var subQ6=sQuery(id+"F17.wireOp",EDGE,"E15.left");Q0=makeQuery(id+"F17.imprint","IMPRINT",FACE,{"disambiguationData":[TD([[makeQuery(id+"F17.imprint","IMPRINT",EDGE,{"derivedFrom":subQ6}),-1.0]])]});}
            var Q1;
            {var subQ5=sQuery(id+"F17.wireOp",EDGE,"E15.right");Q1=makeQuery(id+"F17.imprint","IMPRINT",FACE,{"disambiguationData":[TD([[makeQuery(id+"F17.imprint","IMPRINT",EDGE,{"derivedFrom":subQ5}),-1.0]])]});}
            var Q2;
            {var subQ4=sQuery(id+"F17.wireOp",EDGE,"E16.0.1.3");Q2=makeQuery(id+"F17.imprint","IMPRINT",FACE,{"disambiguationData":[TD([[makeQuery(id+"F17.imprint","IMPRINT",EDGE,{"derivedFrom":subQ4}),-1.0]])]});}
            var Q3;
            {var subQ0=sQuery(id+"F17.wireOp",EDGE,"E16.0.1.1");Q3=makeQuery(id+"F17.imprint","IMPRINT",FACE,{"disambiguationData":[TD([[makeQuery(id+"F17.imprint","IMPRINT",EDGE,{"derivedFrom":subQ0}),-1.0]])]});}
            var Q4;
            {var subQ5=sQuery(id+"F17.wireOp",EDGE,"E16.0.2.3");Q4=makeQuery(id+"F17.imprint","IMPRINT",FACE,{"disambiguationData":[TD([[makeQuery(id+"F17.imprint","IMPRINT",EDGE,{"derivedFrom":subQ5}),-1.0]])]});}
            var Q5;
            {var subQ5=sQuery(id+"F17.wireOp",EDGE,"E16.0.2.1");Q5=makeQuery(id+"F17.imprint","IMPRINT",FACE,{"disambiguationData":[TD([[makeQuery(id+"F17.imprint","IMPRINT",EDGE,{"derivedFrom":subQ5}),-1.0]])]});}
            var Q6;
            {var subQ6=sQuery(id+"F17.wireOp",EDGE,"E16.0.3.3");Q6=makeQuery(id+"F17.imprint","IMPRINT",FACE,{"disambiguationData":[TD([[makeQuery(id+"F17.imprint","IMPRINT",EDGE,{"derivedFrom":subQ6}),-1.0]])]});}
            var Q7;
            {var subQ5=sQuery(id+"F17.wireOp",EDGE,"E16.0.3.1");Q7=makeQuery(id+"F17.imprint","IMPRINT",FACE,{"disambiguationData":[TD([[makeQuery(id+"F17.imprint","IMPRINT",EDGE,{"derivedFrom":subQ5}),-1.0]])]});}
            extrude(context, id + "F18", {"entities" : qUnion([Q0, Q1, Q2, Q3, Q4, Q5, Q6, Q7]), "depth" : 1950 * mm});
        }
        {
            var Q0;
            Q0=makeQuery(id+"F10.opExtrude","SWEPT_FACE",FACE,{"disambiguationData":[OSD([sQuery(id+"F9.wireOp",EDGE,"E10.right")])]});
            var sketch = newSketch(context, id + "F19", { "sketchPlane" : qUnion([Q0])});
            skLineSegment(sketch, "E17.bottom", {"start": v(-5440, 2180) * mm, "end": v(-5315, 2180) * mm});
            skLineSegment(sketch, "E17.top", {"start": v(-5440, 2130) * mm, "end": v(-5315, 2130) * mm});
            skLineSegment(sketch, "E17.left", {"start": v(-5440, 2180) * mm, "end": v(-5440, 2130) * mm});
            skLineSegment(sketch, "E17.right", {"start": v(-5315, 2180) * mm, "end": v(-5315, 2130) * mm});
            skSolve(sketch);
        }
        {
            var Q0;
            Q0=makeQuery(id+"F19.imprint","IMPRINT",FACE,{"disambiguationData":[TD([[makeQuery(id+"F19.imprint","IMPRINT",EDGE,{"derivedFrom":sQuery(id+"F19.wireOp",EDGE,"E17.bottom")}),-1.0]])]});
            extrude(context, id + "F20", {"entities" : qUnion([Q0]), "depth" : 1385 * mm});
        }
        {
            var Q0;
            Q0=makeQuery(id+"F20.opExtrude","SWEPT_FACE",FACE,{"disambiguationData":[OSD([sQuery(id+"F19.wireOp",EDGE,"E17.bottom")])]});
            var sketch = newSketch(context, id + "F21", { "sketchPlane" : qUnion([Q0])});
            skLineSegment(sketch, "E18", {"start": v(5440, -1990) * mm, "end": v(4365, 0) * mm});
            skLineSegment(sketch, "E19", {"start": v(4365, 0) * mm, "end": v(4233.03, -71.3) * mm});
            skLineSegment(sketch, "E20", {"start": v(4233.03, -71.3) * mm, "end": v(5308.03, -2061.3) * mm});
            skLineSegment(sketch, "E21", {"start": v(5308.03, -2061.3) * mm, "end": v(5440, -1990) * mm});
            skLineSegment(sketch, "E22", {"start": v(5416.24, -1946) * mm, "end": v(5284.26, -2017.3) * mm});
            skLineSegment(sketch, "E23", {"start": v(4256.79, -115.28) * mm, "end": v(4388.76, -44) * mm});
            skSolve(sketch);
        }
        {
            var Q0;
            {var subQ2=sQuery(id+"F21.wireOp",EDGE,"E22");var subQ4=sQuery(id+"F21.wireOp",EDGE,"E18");var subQ6=makeQuery(id+"F21.imprint","INTERSECT",VERTEX,{"derivedFrom":[subQ4,subQ2]});Q0=makeQuery(id+"F21.imprint","IMPRINT",FACE,{"disambiguationData":[TD([[makeQuery(id+"F21.imprint","IMPRINT",EDGE,{"disambiguationData":[TD([[subQ6,-1.0]])],"derivedFrom":subQ2}),1.0]])]});}
            var Q1;
            {var subQ0=sQuery(id+"F19.wireOp",EDGE,"E17.bottom");var subQ1=makeQuery(id+"F20.opExtrude","CAP_EDGE",EDGE,{"disambiguationData":[OSD([subQ0])],"isStart":false});var subQ2=sQuery(id+"F21.wireOp",EDGE,"E22");var subQ3=makeQuery(id+"F21.imprint","INTERSECT",VERTEX,{"derivedFrom":[subQ1,subQ2]});Q1=makeQuery(id+"F21.imprint","IMPRINT",FACE,{"disambiguationData":[TD([[makeQuery(id+"F21.imprint","IMPRINT",EDGE,{"disambiguationData":[TD([[subQ3,1.0]])],"derivedFrom":subQ1}),1.0]])]});}
            var Q2;
            {var subQ3=sQuery(id+"F21.wireOp",EDGE,"E21");var subQ5=sQuery(id+"F21.wireOp",EDGE,"E20");var subQ7=makeQuery(id+"F21.imprint","INTERSECT",VERTEX,{"derivedFrom":[subQ5,subQ3]});Q2=makeQuery(id+"F21.imprint","IMPRINT",FACE,{"disambiguationData":[TD([[makeQuery(id+"F21.imprint","IMPRINT",EDGE,{"disambiguationData":[TD([[subQ7,1.0]])],"derivedFrom":subQ5}),1.0]])]});}
            var Q3;
            {var subQ2=sQuery(id+"F21.wireOp",EDGE,"E19");Q3=makeQuery(id+"F21.imprint","IMPRINT",FACE,{"disambiguationData":[TD([[makeQuery(id+"F21.imprint","IMPRINT",EDGE,{"derivedFrom":subQ2}),1.0]])]});}
            extrude(context, id + "F22", {"entities" : qUnion([Q0, Q1, Q2, Q3]), "oppositeDirection" : true, "depth" : 2000 * mm});
        }
        {
            var Q0;
            {var subQ7=sQuery(id+"F21.wireOp",EDGE,"E23");Q0=makeQuery(id+"F21.imprint","IMPRINT",FACE,{"disambiguationData":[TD([[makeQuery(id+"F21.imprint","IMPRINT",EDGE,{"derivedFrom":subQ7}),-1.0]])]});}
            extrude(context, id + "F23", {"entities" : qUnion([Q0]), "operationType" : NewBodyOperationType.ADD, "oppositeDirection" : true, "depth" : 50 * mm});
        }
        {
            var Q0;
            Q0=makeQuery(id+"F7.opExtrude","CAP_FACE",FACE,{"disambiguationData":[OSD([sQuery(id+"F3.wireOp",EDGE,"E6.bottom"),sQuery(id+"F3.wireOp",EDGE,"E6.top"),sQuery(id+"F3.wireOp",EDGE,"E6.left"),sQuery(id+"F3.wireOp",EDGE,"E9.right")])],"isStart":false});
            var sketch = newSketch(context, id + "F24", { "sketchPlane" : qUnion([Q0])});
            skLineSegment(sketch, "E24.bottom", {"start": v(5440, -3520) * mm, "end": v(5460, -3520) * mm});
            skLineSegment(sketch, "E24.top", {"start": v(5440, -1990) * mm, "end": v(5460, -1990) * mm});
            skLineSegment(sketch, "E24.left", {"start": v(5440, -3520) * mm, "end": v(5440, -1990) * mm});
            skLineSegment(sketch, "E24.right", {"start": v(5460, -3520) * mm, "end": v(5460, -1990) * mm});
            skSolve(sketch);
        }
        {
            var Q0;
            {var subQ0=sQuery(id+"F24.wireOp",EDGE,"E24.bottom");Q0=makeQuery(id+"F24.imprint","IMPRINT",FACE,{"disambiguationData":[TD([[makeQuery(id+"F24.imprint","IMPRINT",EDGE,{"derivedFrom":subQ0}),1.0]])]});}
            extrude(context, id + "F25", {"entities" : qUnion([Q0]), "oppositeDirection" : true, "depth" : 2050 * mm});
        }
        {
            var Q0;
            Q0=makeQuery(id+"F8.opExtrude","CAP_FACE",FACE,{"disambiguationData":[OSD([sQuery(id+"F3.wireOp",EDGE,"E9.bottom"),sQuery(id+"F3.wireOp",EDGE,"E9.top"),sQuery(id+"F3.wireOp",EDGE,"E9.left"),sQuery(id+"F3.wireOp",EDGE,"E9.right")])],"isStart":false});
            var sketch = newSketch(context, id + "F26", { "sketchPlane" : qUnion([Q0])});
            skLineSegment(sketch, "E25.bottom", {"start": v(-20, -0.02) * mm, "end": v(4365, -0.02) * mm});
            skLineSegment(sketch, "E25.top", {"start": v(-20, 19.98) * mm, "end": v(4365, 19.98) * mm});
            skLineSegment(sketch, "E25.left", {"start": v(-20, -0.02) * mm, "end": v(-20, 19.98) * mm});
            skLineSegment(sketch, "E25.right", {"start": v(4365, -0.02) * mm, "end": v(4365, 19.98) * mm});
            skSolve(sketch);
        }
        {
            var Q0;
            Q0=makeQuery(id+"F26.imprint","IMPRINT",FACE,{"disambiguationData":[TD([[makeQuery(id+"F26.imprint","IMPRINT",EDGE,{"derivedFrom":sQuery(id+"F26.wireOp",EDGE,"E25.top")}),-1.0]])]});
            extrude(context, id + "F27", {"entities" : qUnion([Q0]), "oppositeDirection" : true, "depth" : 2050 * mm});
        }
        {
            var Q0;
            Q0=makeQuery(id+"F12.opExtrude","SWEPT_FACE",FACE,{"disambiguationData":[OSD([sQuery(id+"F11.wireOp",EDGE,"E11.bottom")])]});
            var sketch = newSketch(context, id + "F28", { "sketchPlane" : qUnion([Q0])});
            skLineSegment(sketch, "E26", {"start": v(5460, -3520) * mm, "end": v(-20, -3520) * mm});
            skLineSegment(sketch, "E27", {"start": v(-20, -3520) * mm, "end": v(-20, 19.98) * mm});
            skLineSegment(sketch, "E28", {"start": v(-20, 19.98) * mm, "end": v(4365, 19.98) * mm});
            skLineSegment(sketch, "E29", {"start": v(4365, 19.98) * mm, "end": v(5460, -1990) * mm});
            skLineSegment(sketch, "E30", {"start": v(5460, -1990) * mm, "end": v(5460, -3520) * mm});
            skLineSegment(sketch, "E31.0", {"start": v(5510, -3570) * mm, "end": v(-70, -3570) * mm});
            skLineSegment(sketch, "E31.1", {"start": v(5510, -1977.26) * mm, "end": v(5510, -3570) * mm});
            skLineSegment(sketch, "E31.2", {"start": v(4394.7, 69.98) * mm, "end": v(5510, -1977.26) * mm});
            skLineSegment(sketch, "E31.3", {"start": v(-70, 69.98) * mm, "end": v(4394.7, 69.98) * mm});
            skLineSegment(sketch, "E32.0", {"start": v(-70, -3570) * mm, "end": v(-70, 69.98) * mm});
            skSolve(sketch);
        }
        {
            var Q0;
            Q0=makeQuery(id+"F28.imprint","IMPRINT",FACE,{"disambiguationData":[TD([[makeQuery(id+"F28.imprint","IMPRINT",EDGE,{"derivedFrom":sQuery(id+"F28.wireOp",EDGE,"E26")}),1.0]])]});
            var Q1;
            Q1=makeQuery(id+"F28.imprint","IMPRINT",FACE,{"disambiguationData":[TD([[makeQuery(id+"F28.imprint","IMPRINT",EDGE,{"derivedFrom":sQuery(id+"F28.wireOp",EDGE,"E26")}),-1.0]])]});
            var Q2;
            {var subQ0=sQuery(id+"F11.wireOp",EDGE,"E11.bottom");Q2=makeQuery(id+"F28.imprint","IMPRINT",FACE,{"disambiguationData":[TD([[makeQuery(id+"F28.imprint","IMPRINT",EDGE,{"derivedFrom":makeQuery(id+"F12.opExtrude","CAP_EDGE",EDGE,{"disambiguationData":[OSD([subQ0])],"isStart":true})}),-1.0]])]});}
            extrude(context, id + "F29", {"entities" : qUnion([Q0, Q1, Q2]), "depth" : 500 * mm, "hasDraft" : true, "draftAngle" : 68.5 * degree, "draftPullDirection" : true, "hasSecondDirection" : true, "secondDirectionOppositeDirection" : false, "secondDirectionDepth" : 20 * mm, "hasSecondDirectionDraft" : true, "secondDirectionDraftAngle" : 68.5 * degree});
        }
        {
            var Q0;
            Q0=makeQuery(id+"F29.opExtrude","CAP_FACE",FACE,{"disambiguationData":[OSD([sQuery(id+"F28.wireOp",EDGE,"E31.0"),sQuery(id+"F28.wireOp",EDGE,"E31.1"),sQuery(id+"F28.wireOp",EDGE,"E31.2"),sQuery(id+"F28.wireOp",EDGE,"E31.3"),sQuery(id+"F28.wireOp",EDGE,"E32.0")])],"isStart":true});
            shell(context, id + "F30", {"entities" : qUnion([Q0]), "thickness" : 20 * mm});
        }
        {
            var Q0;
            Q0=makeQuery(id+"F29.opExtrude","CAP_FACE",FACE,{"disambiguationData":[OSD([sQuery(id+"F28.wireOp",EDGE,"E31.0"),sQuery(id+"F28.wireOp",EDGE,"E31.1"),sQuery(id+"F28.wireOp",EDGE,"E31.2"),sQuery(id+"F28.wireOp",EDGE,"E31.3"),sQuery(id+"F28.wireOp",EDGE,"E32.0")])],"isStart":false});
            var sketch = newSketch(context, id + "F31", { "sketchPlane" : qUnion([Q0])});
            skLineSegment(sketch, "E33.0", {"start": v(1199.32, -1199.34) * mm, "end": v(3640.74, -1199.34) * mm});
            skLineSegment(sketch, "E34.0", {"start": v(1199.32, -2300.68) * mm, "end": v(1199.32, -1199.34) * mm});
            skLineSegment(sketch, "E35.0", {"start": v(4240.68, -2300.68) * mm, "end": v(1199.32, -2300.68) * mm});
            skLineSegment(sketch, "E36.0", {"start": v(3640.74, -1199.34) * mm, "end": v(4240.68, -2300.58) * mm});
            skLineSegment(sketch, "E37.bottom", {"start": v(1249.32, -2250.68) * mm, "end": v(2249.32, -2250.68) * mm});
            skLineSegment(sketch, "E37.top", {"start": v(1249.32, -1250.68) * mm, "end": v(2249.32, -1250.68) * mm});
            skLineSegment(sketch, "E37.left", {"start": v(1249.32, -2250.68) * mm, "end": v(1249.32, -1250.68) * mm});
            skLineSegment(sketch, "E37.right", {"start": v(2249.32, -2250.68) * mm, "end": v(2249.32, -1250.68) * mm});
            skLineSegment(sketch, "E38.1.0.0", {"start": v(2528.38, -1250.56) * mm, "end": v(3528.38, -1250.56) * mm});
            skLineSegment(sketch, "E38.1.0.1", {"start": v(2528.38, -2250.56) * mm, "end": v(2528.38, -1250.56) * mm});
            skLineSegment(sketch, "E38.1.0.2", {"start": v(2528.38, -2250.56) * mm, "end": v(3528.38, -2250.56) * mm});
            skLineSegment(sketch, "E38.1.0.3", {"start": v(3528.38, -2250.56) * mm, "end": v(3528.38, -1250.56) * mm});
            skLineSegment(sketch, "E38.direction1", {"start": v(1249.32, -2250.68) * mm, "end": v(2528.38, -2250.56) * mm, "construction": true});
            skSolve(sketch);
        }
        {
            var Q0;
            Q0=makeQuery(id+"F31.imprint","IMPRINT",FACE,{"disambiguationData":[TD([[makeQuery(id+"F31.imprint","IMPRINT",EDGE,{"derivedFrom":sQuery(id+"F31.wireOp",EDGE,"E38.1.0.0")}),-1.0]])]});
            var Q1;
            Q1=makeQuery(id+"F31.imprint","IMPRINT",FACE,{"disambiguationData":[TD([[makeQuery(id+"F31.imprint","IMPRINT",EDGE,{"derivedFrom":sQuery(id+"F31.wireOp",EDGE,"E37.bottom")}),1.0]])]});
            extrude(context, id + "F32", {"entities" : qUnion([Q0, Q1]), "operationType" : NewBodyOperationType.REMOVE, "oppositeDirection" : true, "depth" : 25 * mm});
        }
        {
            var Q0;
            Q0=makeQuery(id+"F25.opExtrude","SWEPT_FACE",FACE,{"disambiguationData":[OSD([sQuery(id+"F24.wireOp",EDGE,"E24.right")])]});
            var sketch = newSketch(context, id + "F33", { "sketchPlane" : qUnion([Q0])});
            skLineSegment(sketch, "E39.bottom", {"start": v(-3291.91, 1093.14) * mm, "end": v(-2191.91, 1093.14) * mm});
            skLineSegment(sketch, "E39.top", {"start": v(-3291.91, 2093.14) * mm, "end": v(-2191.91, 2093.14) * mm});
            skLineSegment(sketch, "E39.left", {"start": v(-3291.91, 1093.14) * mm, "end": v(-3291.91, 2093.14) * mm});
            skLineSegment(sketch, "E39.right", {"start": v(-2191.91, 1093.14) * mm, "end": v(-2191.91, 2093.14) * mm});
            skSolve(sketch);
        }
        {
            var Q0;
            Q0 = qSketchRegion(id + "F33", true);
            extrude(context, id + "F34", {"entities" : qUnion([Q0]), "operationType" : NewBodyOperationType.REMOVE, "oppositeDirection" : true, "depth" : 2000 * mm});
        }
        {
            var Q0;
            Q0=makeQuery(id+"F27.opExtrude","SWEPT_FACE",FACE,{"disambiguationData":[OSD([sQuery(id+"F26.wireOp",EDGE,"E25.top")])]});
            var sketch = newSketch(context, id + "F35", { "sketchPlane" : qUnion([Q0])});
            skPoint(sketch, "E40.firstSnap0", {"position": v(-4365, 1084.35) * mm});
            skLineSegment(sketch, "E40.bottom", {"start": v(-4054.6, 1084.35) * mm, "end": v(-2654.6, 1084.35) * mm});
            skLineSegment(sketch, "E40.top", {"start": v(-4054.6, 2084.35) * mm, "end": v(-2654.6, 2084.35) * mm});
            skLineSegment(sketch, "E40.left", {"start": v(-4054.6, 1084.35) * mm, "end": v(-4054.6, 2084.35) * mm});
            skLineSegment(sketch, "E40.right", {"start": v(-2654.6, 1084.35) * mm, "end": v(-2654.6, 2084.35) * mm});
            skSolve(sketch);
        }
        {
            var Q0;
            Q0 = qSketchRegion(id + "F35", true);
            extrude(context, id + "F36", {"entities" : qUnion([Q0]), "operationType" : NewBodyOperationType.REMOVE, "oppositeDirection" : true, "depth" : 2000 * mm});
        }
    });
